# Revit family: LAMP_KOMBIC 200 SQ DALI
name_source: partatom
category: Luminarias
revit_build: Autodesk Revit 2018 (Build: 20190510_1515(x64)
units: mm (PartAtom-declared; Revit-internal decimal feet)

## family parameters
Anfitrión = Techo
Compartido = No
Corte con vacíos al cargar = No
Cota de conector redondo = Diámetro de uso
Número OmniClass = 23.80.70.11
Origen de luz = Sí
Punto de cálculo de habitación = No
Siempre vertical = Sí
Tipo de pieza = Normal
Título OmniClass = Luminaries for Internal Lighting

## types (6) — shared parameters
Altura total = 106 mm  [stored 0.347769 ft]
CRI = 80
Cambio de temperatura de color de luz atenuada = <Ninguno>
Comentarios de tipo = Availability of switching between accessories through visibility parameters when placed in a project.
Dimensions = 230x230x106
Fabricante = LAMP
Filtro de color = 16777215
Finish = RAL9010
Gear = Electronic
Height = 106 mm  [stored 0.347769 ft]
IEE = A+
Installation instructions = https://www.lamp.es
Insulation class = II
Last update = 24/02/2022
MacAdam = 3
Manufacturer URL = http://www.lamp.es
Manufacturer country = Spain
Manufacturer name = LAMP
Material Armazón BL = LAMP_PC Armazón Kombic BL
Material Armazón GR = LAMP_PC Armazón Kombic GR
Material Difusor = LAMP_PMMA Difusor Kombic
Material Disipador = LAMP_Aluminio Disipador Kombic
Material Reflector = LAMP_PC Reflector Kombic Metalizado Brillante
Medida exterior = 230 mm  [stored 0.754593 ft]
Medida interior = 188 mm  [stored 0.616798 ft]
Model explanation = Availability of switching between accessories through visibility parameters when placed in a project.
Photobiological risk = Group 0
Power Supply = 220-240V 50/60Hz
Product URL = https://www.lamp.es
Product datasheet = http://www.lamp.es
Protection rating = IP44
Recessed dimensions = 220x220
Ángulo de inclinación = 90.00°

## per-type parameters (varying)
| type | Archivo de red fotométrica | Descripción | Efficacy | LED Lifetime | Lámpara | Modelo | Plum | Power | Product code | Type | Weight |
| 1522LM 3000 BRIGHT BLANCO | K31SQ3040OP830NRW.IES | KOMBIC 200 SQ BRIGHT 3000 WW | 84 lm/W | 50.000 L80 B10 | MID-POWER LED | K31SQ3040OP830DRW | 18 W | 17 W | K31SQ3040OP830DRW | MID POWER TRIDONIC | 0.82 kg |
| 1602LM 4000 BRIGHT BLANCO | K31SQ3040OP840NRW.IES | KOMBIC 200 SQ BRIGHT 3000 NW | 89 lm/W | 50.000 L80 B10 | MID-POWER LED | K31SQ3040OP840DRW | 18 W | 17 W | K31SQ3040OP840DRW | MID POWER TRIDONIC | 0.82 kg |
| 2024LM 3000 BRIGHT BLANCO | K31SQ4040OP830NRW.IES | KOMBIC 200 SQ 4000 IP44 WW OPAL BR/WH | 80 lm/W | 50.000 L80 B10 | MID-POWER LED | K31SQ4040OP830DRW | 25 W | 24 W | K31SQ4040OP830DRW | MID POWER TRIDONIC | 0.82 kg |
| 2131LM 4000 BRIGHT BLANCO | K31SQ4040OP840NRW.IES | KOMBIC 200 SQ 4000 IP44 NW OPAL BR/WH | 84 lm/W | 50.000 L80 B10 | MID-POWER LED | K31SQ4040OP840DRW | 25 W | 24 W | K31SQ4040OP840DRW | MID POWER TRIDONIC | 0.82 kg |
| 3249LM 3000 BRIGHT BLANCO | K31SQ5040OP830NRW.IES | KOMBIC 200 SQ 5000 IP44 WW OPAL BR/WH | 85 lm/W | 50.000 L70 B10 | COB LED | K31SQ5040OP830DRW | 38 W | 36 W | K31SQ5040OP830DRW | COB PHILIPS | 1.54 kg |
| 3494LM 4000 BRIGHT BLANCO | K31SQ5040OP840NRW.IES | KOMBIC 200 SQ 5000 IP44 NW OPAL BR/WH | 92 lm/W | 50.000 L70 B10 | COB LED | K31SQ5040OP840DRW | 38 W | 36 W | K31SQ5040OP840DRW | COB PHILIPS | 1.54 kg |

note: [stored X ft] marks values corroborated as IEEE doubles in the binary element streams (Revit-internal decimal feet)
